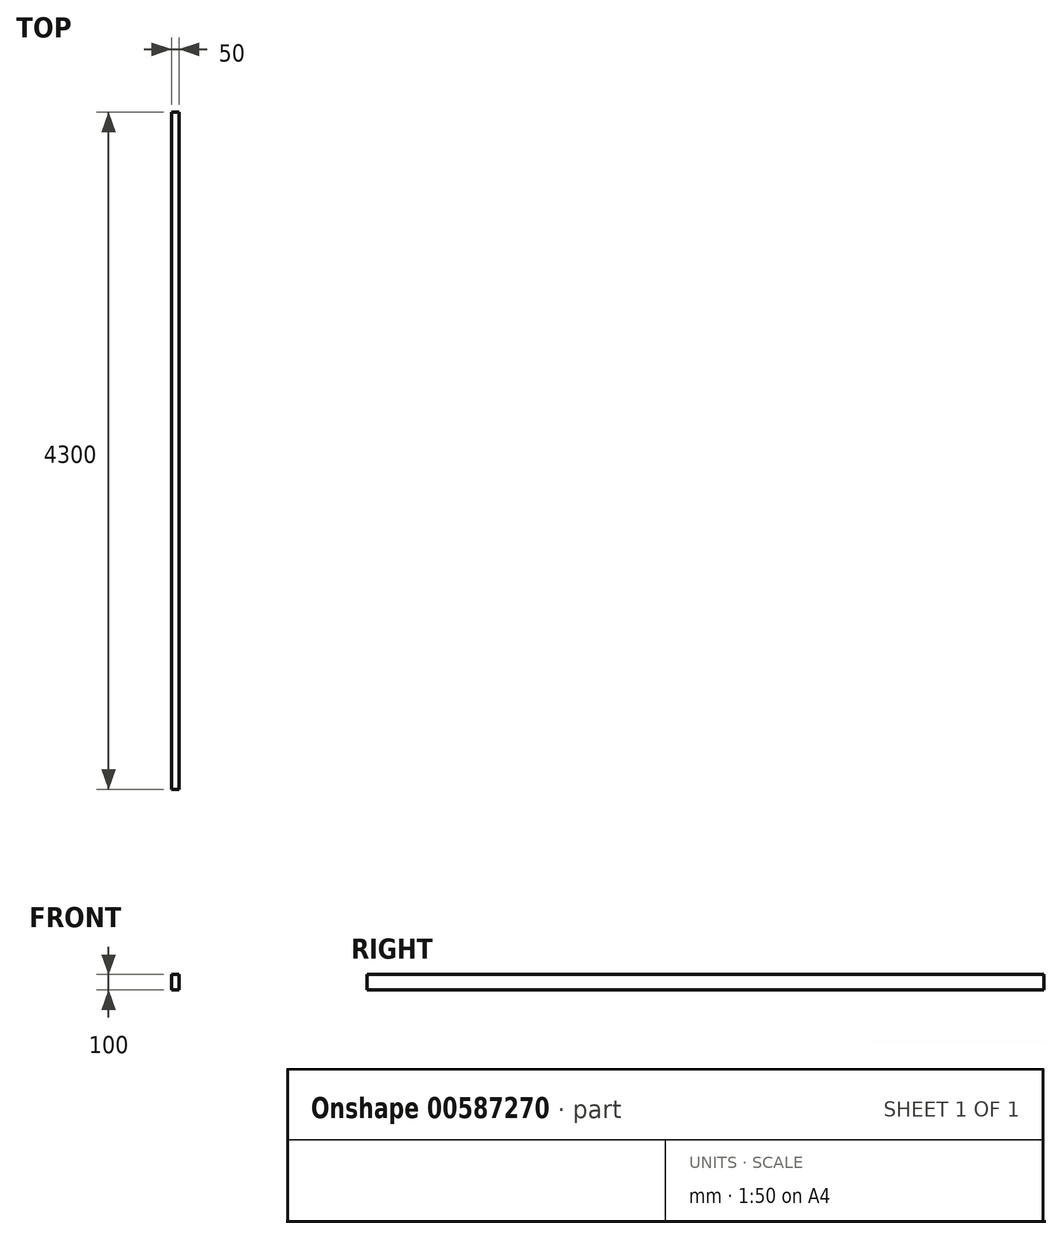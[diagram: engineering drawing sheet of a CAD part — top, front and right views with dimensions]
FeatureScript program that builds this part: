
annotation { "Feature Type Name" : "Feature", "Feature Type Description" : "" }
export const myFeature = defineFeature(function(context is Context, id is Id, definition is map)
    precondition{}
    {
        {
            var Q0;
            Q0=qCreatedBy(makeId("Front.planeOp"),FACE);
            var sketch = newSketch(context, id + "F0", { "sketchPlane" : qUnion([Q0])});
            skLineSegment(sketch, "E0.bottom", {"start": v(25, 50) * mm, "end": v(-25, 50) * mm});
            skLineSegment(sketch, "E0.top", {"start": v(25, -50) * mm, "end": v(-25, -50) * mm});
            skLineSegment(sketch, "E0.left", {"start": v(25, 50) * mm, "end": v(25, -50) * mm});
            skLineSegment(sketch, "E0.right", {"start": v(-25, 50) * mm, "end": v(-25, -50) * mm});
            skPoint(sketch, "E0.middle", {"position": v(0, 0) * mm});
            skSolve(sketch);
        }
        {
            var Q0;
            Q0=makeQuery(id+"F0.imprint","IMPRINT",FACE,{"disambiguationData":[TD([[makeQuery(id+"F0.imprint","IMPRINT",EDGE,{"derivedFrom":sQuery(id+"F0.wireOp",EDGE,"E0.bottom")}),1.0]])]});
            extrude(context, id + "F1", {"entities" : qUnion([Q0]), "endBound" : BoundingType.SYMMETRIC, "depth" : 4300 * mm, "offsetDistance" : 25.4 * mm});
        }
    });
